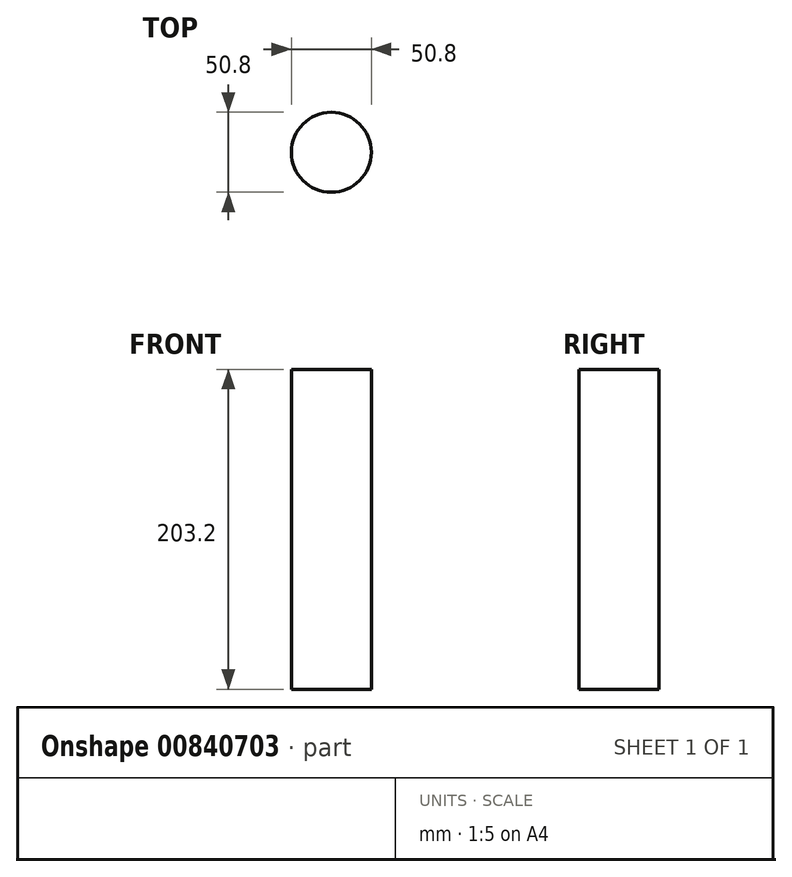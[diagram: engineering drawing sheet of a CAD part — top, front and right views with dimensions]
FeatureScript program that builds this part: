
annotation { "Feature Type Name" : "Feature", "Feature Type Description" : "" }
export const myFeature = defineFeature(function(context is Context, id is Id, definition is map)
    precondition{}
    {
        {
            var Q0;
            Q0=qCreatedBy(makeId("Top.planeOp"),FACE);
            var sketch = newSketch(context, id + "F0", { "sketchPlane" : qUnion([Q0])});
            skCircle(sketch, "E0", {"center": v(0, 0) * mm, "radius": 25.4 * mm});
            skSolve(sketch);
        }
        {
            var Q0;
            Q0=makeQuery(id+"F0.imprint","IMPRINT",FACE,{"disambiguationData":[TD([[makeQuery(id+"F0.imprint","IMPRINT",EDGE,{"derivedFrom":sQuery(id+"F0.wireOp",EDGE,"E0")}),1.0]])]});
            extrude(context, id + "F1", {"entities" : qUnion([Q0]), "depth" : 203.2 * mm, "offsetDistance" : 25.4 * mm});
        }
    });
